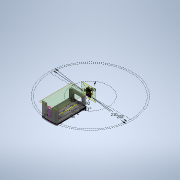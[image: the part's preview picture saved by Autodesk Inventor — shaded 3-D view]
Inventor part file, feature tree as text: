
AUTODESK INVENTOR PART (.ipt)
format: ipt  version: 2020 (Build 240168000, 168)  size: 727,040 bytes
history: native  units: mm
features: projected_geometry x31, extrude x18, sketch x12, fillet x10, other x7, chamfer x2
ambient origin geometry x8: Origin, YZ Plane, XZ Plane, XY Plane, X Axis, Y Axis, Z Axis, Center Point
bodies: Body1 (feature_tree)
feature tree (80):
  other  "Твердое тело1"
  sketch  "Эскиз1"
  extrude  "Выдавливание3"  Depth=202.0mm
  other  "РабПлоскость1"
  extrude  "Выдавливание1"  Depth=35.0mm
  other  "РабПлоскость2"
  sketch  "Эскиз2"
  extrude  "Выдавливание4"  Depth=68.0mm
  extrude  "Выдавливание5"  Depth=2.0mm
  sketch  "Эскиз4"
  extrude  "Выдавливание6"  Depth=2.0mm
  extrude  "Выдавливание7"  Depth=3.0mm
  other  "РабПлоскость3"
  extrude  "Выдавливание8"  Depth=3.0mm
  other  "РабПлоскость4"
  extrude  "Выдавливание9"  Depth=210.0mm
  sketch  "Эскиз8"
  extrude  "Выдавливание10"  Depth=20.0mm TaperAngle=0.0deg
  fillet  "Сопряжение1"  Radius=1.5mm
  fillet  "Сопряжение2"  Radius=28.0mm
  fillet  "Сопряжение3"  Radius=7.0mm
  fillet  "Сопряжение4"  Radius=20.0mm
  fillet  "Сопряжение5"  Radius=13.0mm
  extrude  "Выдавливание11"  Depth=5.0mm
  extrude  "Выдавливание12"  Depth=3.0mm
  fillet  "Сопряжение6"  Radius=10.0mm
  extrude  "Выдавливание13"  Depth=84.0mm
  chamfer  "Фаска1"  Distance=5.0mm
  fillet  "Сопряжение7"  Radius=52.0mm
  sketch  "Эскиз10"
  other  "РабПлоскость5"
  extrude  "Выдавливание14"  Depth=5.0mm TaperAngle=0.0deg
  fillet  "Сопряжение8"  Radius=35.0mm
  extrude  "Выдавливание15"  Depth=18.0mm
  fillet  "Сопряжение9"  Radius=3.0mm
  extrude  "Выдавливание16"  Depth=30.0mm TaperAngle=360.0deg
  fillet  "Сопряжение10"  Radius=0.5mm
  extrude  "Выдавливание17"  TaperAngle=0.0deg  [1 undecoded]
  chamfer  "Фаска2"  Distance=8.0mm
  other  "РабПлоскость7"
  sketch  "Эскиз13"
  extrude  "Выдавливание18"  Depth=2.0mm
  extrude  "Выдавливание19"  Depth=1.5mm TaperAngle=0.0deg
  projected_geometry  "Спроецированная петля1"
  projected_geometry  "Спроецированная петля7"
  projected_geometry  "Спроецированная петля8"
  sketch  "Эскиз3"
  projected_geometry  "Спроецированная петля9"
  projected_geometry  "Спроецированная петля10"
  projected_geometry  "Спроецированная петля11"
  projected_geometry  "Спроецированная петля12"
  sketch  "Эскиз5"
  projected_geometry  "Спроецированная петля13"
  projected_geometry  "Спроецированная петля14"
  projected_geometry  "Спроецированная петля15"
  projected_geometry  "Спроецированная петля16"
  projected_geometry  "Спроецированная петля17"
  sketch  "Эскиз6"
  projected_geometry  "Спроецированная петля18"
  projected_geometry  "Спроецированная петля19"
  projected_geometry  "Спроецированная петля20"
  projected_geometry  "Спроецированная петля21"
  projected_geometry  "Спроецированная петля22"
  projected_geometry  "Спроецированная петля23"
  projected_geometry  "Спроецированная петля24"
  projected_geometry  "Спроецированная петля25"
  projected_geometry  "Спроецированная петля26"
  projected_geometry  "Спроецированная петля27"
  projected_geometry  "Спроецированная петля28"
  sketch  "Эскиз9"
  projected_geometry  "Спроецированная петля29"
  projected_geometry  "Спроецированная петля30"
  sketch  "Эскиз11"
  projected_geometry  "Спроецированная петля31"
  projected_geometry  "Спроецированная петля32"
  projected_geometry  "Спроецированная петля33"
  sketch  "Эскиз12"
  projected_geometry  "Спроецированная петля34"
  projected_geometry  "Спроецированная петля35"
  projected_geometry  "Спроецированная петля36"
note: 1 required parameter value undecoded (feature->parameter linkage not recoverable at this tier; creation-order binding heuristic only, values carry confidence <= 0.55)
